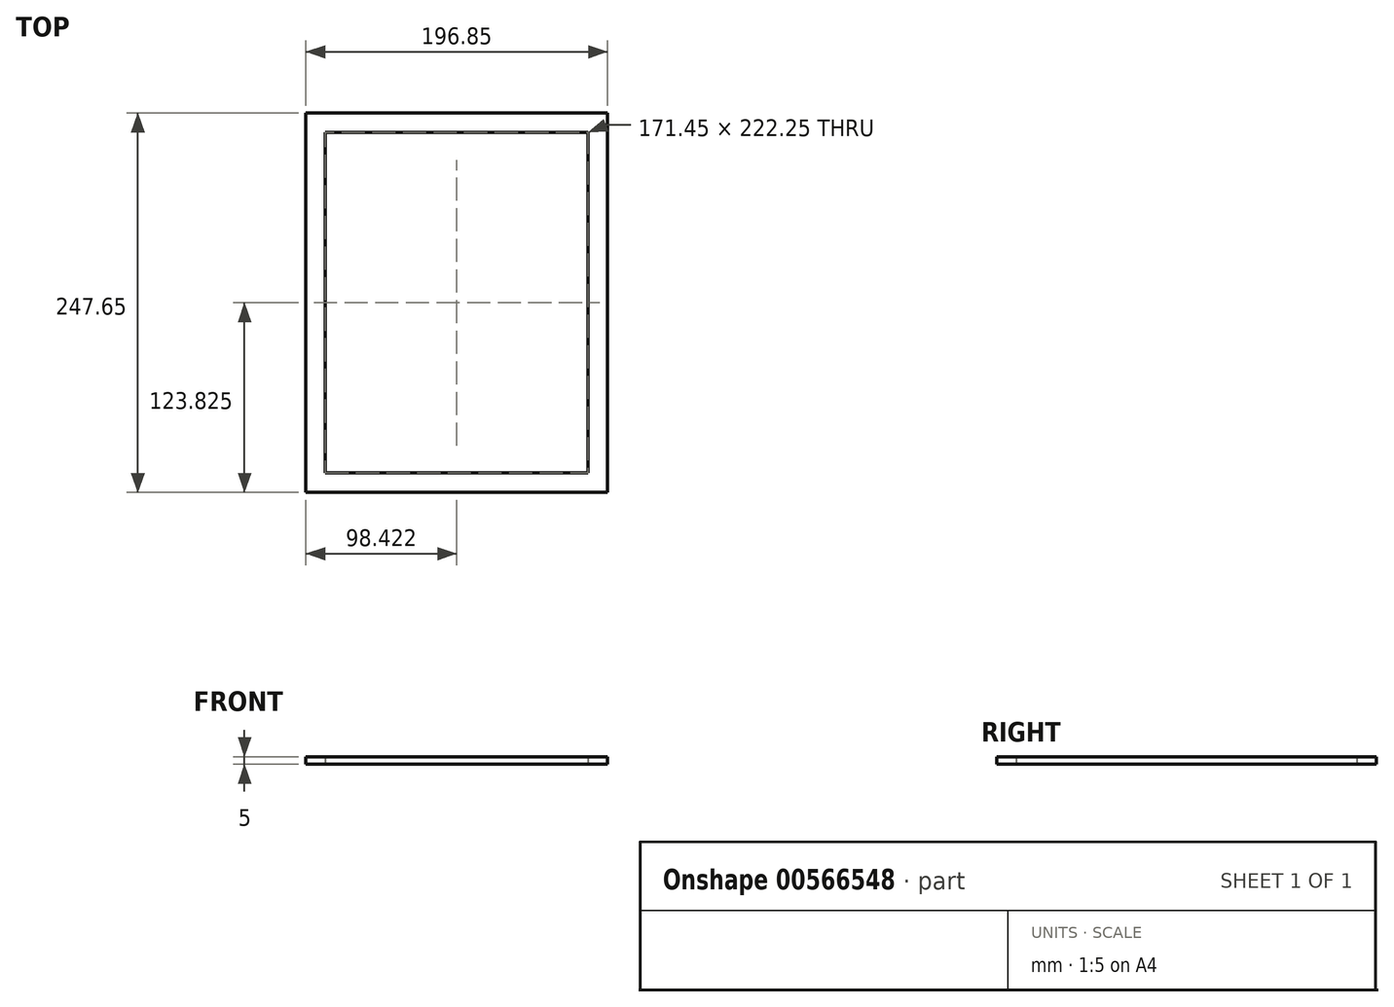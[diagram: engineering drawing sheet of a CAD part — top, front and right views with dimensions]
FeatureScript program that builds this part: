
annotation { "Feature Type Name" : "Feature", "Feature Type Description" : "" }
export const myFeature = defineFeature(function(context is Context, id is Id, definition is map)
    precondition{}
    {
        {
            var Q0;
            Q0=qCreatedBy(makeId("Top.planeOp"),FACE);
            var sketch = newSketch(context, id + "F0", { "sketchPlane" : qUnion([Q0])});
            skLineSegment(sketch, "E0.bottom", {"start": v(-98.45, 144.85) * mm, "end": v(98.4, 144.85) * mm});
            skLineSegment(sketch, "E0.top", {"start": v(-98.45, -102.8) * mm, "end": v(98.4, -102.8) * mm});
            skLineSegment(sketch, "E0.left", {"start": v(-98.45, 144.85) * mm, "end": v(-98.45, -102.8) * mm});
            skLineSegment(sketch, "E0.right", {"start": v(98.4, 144.85) * mm, "end": v(98.4, -102.8) * mm});
            skLineSegment(sketch, "E1.bottom", {"start": v(85.7, -90.1) * mm, "end": v(-85.75, -90.1) * mm});
            skLineSegment(sketch, "E1.top", {"start": v(85.7, 132.15) * mm, "end": v(-85.75, 132.15) * mm});
            skLineSegment(sketch, "E1.left", {"start": v(85.7, -90.1) * mm, "end": v(85.7, 132.15) * mm});
            skLineSegment(sketch, "E1.right", {"start": v(-85.75, -90.1) * mm, "end": v(-85.75, 132.15) * mm});
            skSolve(sketch);
        }
        {
            var Q0;
            Q0=makeQuery(id+"F0.imprint","IMPRINT",FACE,{"disambiguationData":[TD([[makeQuery(id+"F0.imprint","IMPRINT",EDGE,{"derivedFrom":sQuery(id+"F0.wireOp",EDGE,"E1.bottom")}),-1.0]])]});
            var Q1;
            Q1=makeQuery(id+"F0.imprint","IMPRINT",FACE,{"disambiguationData":[TD([[makeQuery(id+"F0.imprint","IMPRINT",EDGE,{"derivedFrom":sQuery(id+"F0.wireOp",EDGE,"E0.bottom")}),-1.0]])]});
            var Q2;
            Q2=sQuery(id+"F0.wireOp",EDGE,"E0.bottom");
            var Q3;
            Q3=sQuery(id+"F0.wireOp",EDGE,"E0.left");
            var Q4;
            Q4=sQuery(id+"F0.wireOp",EDGE,"E0.right");
            var Q5;
            Q5=sQuery(id+"F0.wireOp",EDGE,"E0.top");
            extrude(context, id + "F1", {"entities" : qUnion([Q0, Q1]), "surfaceEntities" : qUnion([Q2, Q3, Q4, Q5]), "depth" : 5 * mm, "offsetDistance" : 25.4 * mm});
        }
        {
            var Q0;
            Q0=makeQuery(id+"F0.imprint","IMPRINT",FACE,{"disambiguationData":[TD([[makeQuery(id+"F0.imprint","IMPRINT",EDGE,{"derivedFrom":sQuery(id+"F0.wireOp",EDGE,"E1.bottom")}),-1.0]])]});
            extrude(context, id + "F2", {"entities" : qUnion([Q0]), "operationType" : NewBodyOperationType.REMOVE, "depth" : 5 * mm, "offsetDistance" : 25.4 * mm});
        }
    });
